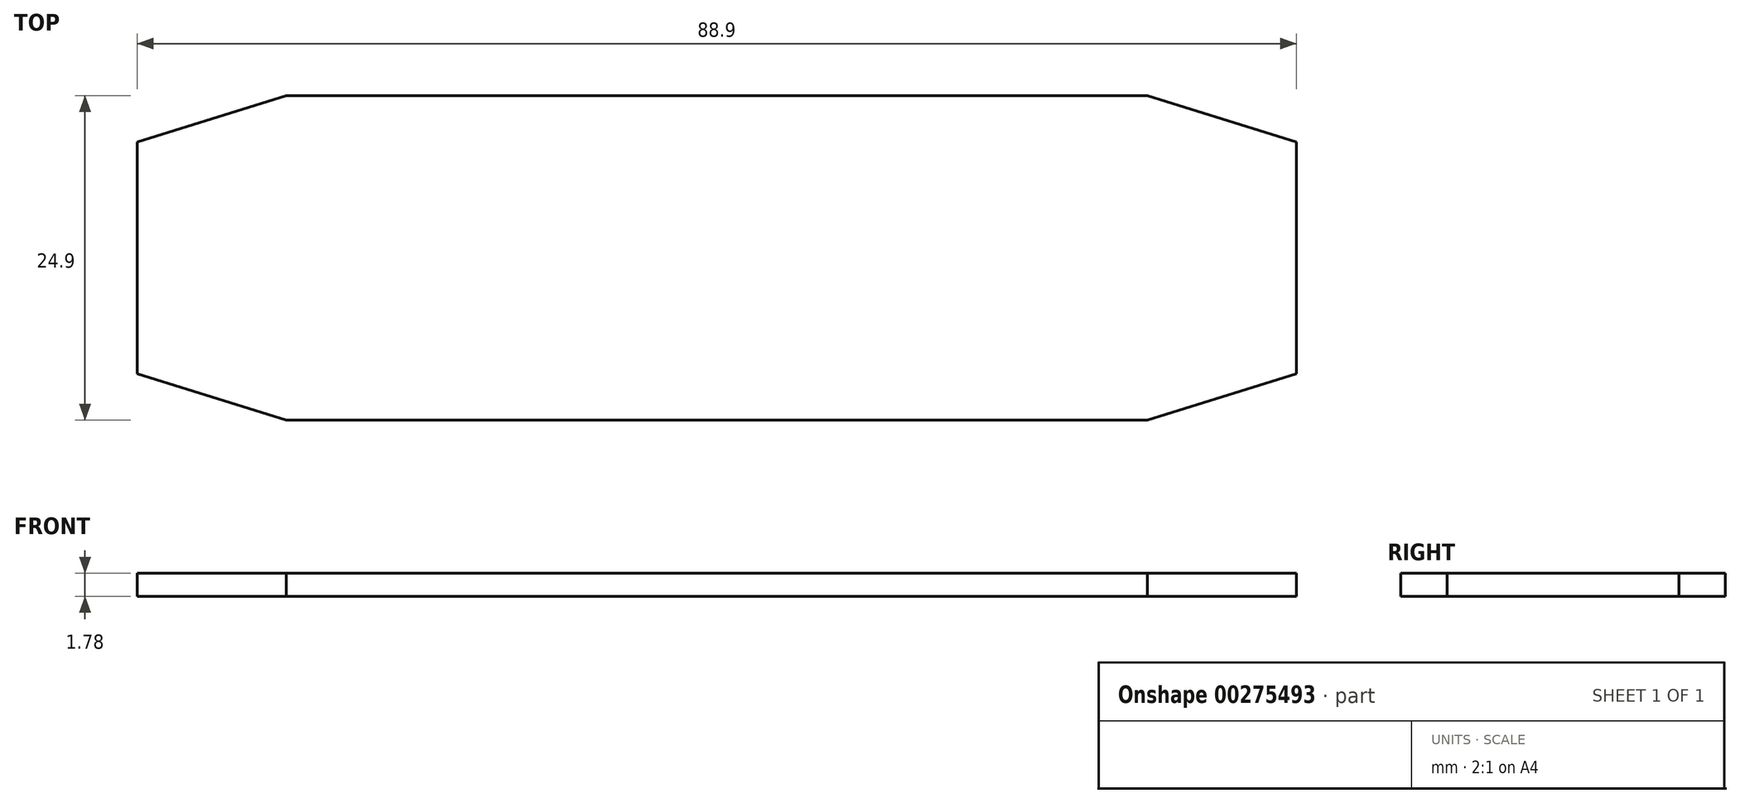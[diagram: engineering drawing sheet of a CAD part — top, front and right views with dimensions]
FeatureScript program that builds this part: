
annotation { "Feature Type Name" : "Feature", "Feature Type Description" : "" }
export const myFeature = defineFeature(function(context is Context, id is Id, definition is map)
    precondition{}
    {
        {
            var Q0;
            Q0=qCreatedBy(makeId("Top.planeOp"),FACE);
            var sketch = newSketch(context, id + "F0", { "sketchPlane" : qUnion([Q0])});
            skLineSegment(sketch, "E0", {"start": v(0, 21.75) * mm, "end": v(0, -21.75) * mm, "construction": true});
            skLineSegment(sketch, "E1", {"start": v(0, 12.45) * mm, "end": v(-33.02, 12.45) * mm});
            skLineSegment(sketch, "E2", {"start": v(-33.02, 12.45) * mm, "end": v(-44.45, 8.89) * mm});
            skLineSegment(sketch, "E3", {"start": v(-44.45, 8.89) * mm, "end": v(-44.45, 0) * mm});
            skLineSegment(sketch, "E4", {"start": v(40.32, 0) * mm, "end": v(-59.06, 0) * mm, "construction": true});
            skLineSegment(sketch, "E5.MirrorCS", {"start": v(44.45, 8.9) * mm, "end": v(44.45, 0) * mm});
            skLineSegment(sketch, "E6.MirrorCS", {"start": v(33.02, 12.45) * mm, "end": v(44.45, 8.9) * mm});
            skLineSegment(sketch, "E7.MirrorCS", {"start": v(0, 12.45) * mm, "end": v(33.02, 12.45) * mm});
            skLineSegment(sketch, "E8.MirrorCS", {"start": v(-44.45, -8.9) * mm, "end": v(-44.45, 0) * mm});
            skLineSegment(sketch, "E9.MirrorCS", {"start": v(-33.02, -12.45) * mm, "end": v(-44.45, -8.9) * mm});
            skLineSegment(sketch, "E10.MirrorCS", {"start": v(0, -12.45) * mm, "end": v(-33.02, -12.45) * mm});
            skLineSegment(sketch, "E11.MirrorCS", {"start": v(0, -12.45) * mm, "end": v(33.02, -12.45) * mm});
            skLineSegment(sketch, "E12.MirrorCS", {"start": v(33.02, -12.45) * mm, "end": v(44.45, -8.9) * mm});
            skLineSegment(sketch, "E13.MirrorCS", {"start": v(44.45, -8.9) * mm, "end": v(44.45, 0) * mm});
            skSolve(sketch);
        }
        {
            var Q0;
            Q0 = qSketchRegion(id + "F0", true);
            extrude(context, id + "F1", {"entities" : qUnion([Q0]), "depth" : 1.78 * mm});
        }
    });
